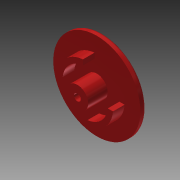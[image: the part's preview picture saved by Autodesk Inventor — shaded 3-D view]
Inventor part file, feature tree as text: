
AUTODESK INVENTOR PART (.ipt)
format: ipt  version: 2014 (Build 180170000, 170)  size: 128,000 bytes
history: native  units: in
note: dims shown in document units (in); Inventor stores cm internally (conversion verified against a paired STEP export)
features: extrude x4, sketch x4, pattern_circular x1, fillet x1
ambient origin geometry x8: Origin, YZ Plane, XZ Plane, XY Plane, X Axis, Y Axis, Z Axis, Center Point
bodies: Solid1 (feature_tree)
feature tree (10):
  extrude  "Extrusion1"  Depth=0.1in TaperAngle=0.0deg
  extrude  "Extrusion2"  Depth=0.335in TaperAngle=0.0deg
  extrude  "Extrusion3"  Depth=0.335in TaperAngle=0.0deg
  extrude  "Extrusion4"  Depth=0.05in
  pattern_circular  "Circular Pattern1"  [2 undecoded]
  fillet  "Fillet1"  Radius=0.48in
  sketch  "Sketch1"  dims[d0=1.5in d1=0.1in d2=0.0in]
  sketch  "Sketch2"  dims[d3=0.373in d4=0.335in d5=0.0in]
  sketch  "Sketch3"  dims[d6=0.1195in d7=0.335in d8=0.0in]
  sketch  "Sketch4"  dims[d9=0.039in d10=0.039in d11=0.39in d12=0.48in d13=0.2in d14=0.0in d15=0.7874in d16=360.0deg d18=0.05in]
note: 2 required parameter values undecoded (feature->parameter linkage not recoverable at this tier; creation-order binding heuristic only, values carry confidence <= 0.55)
